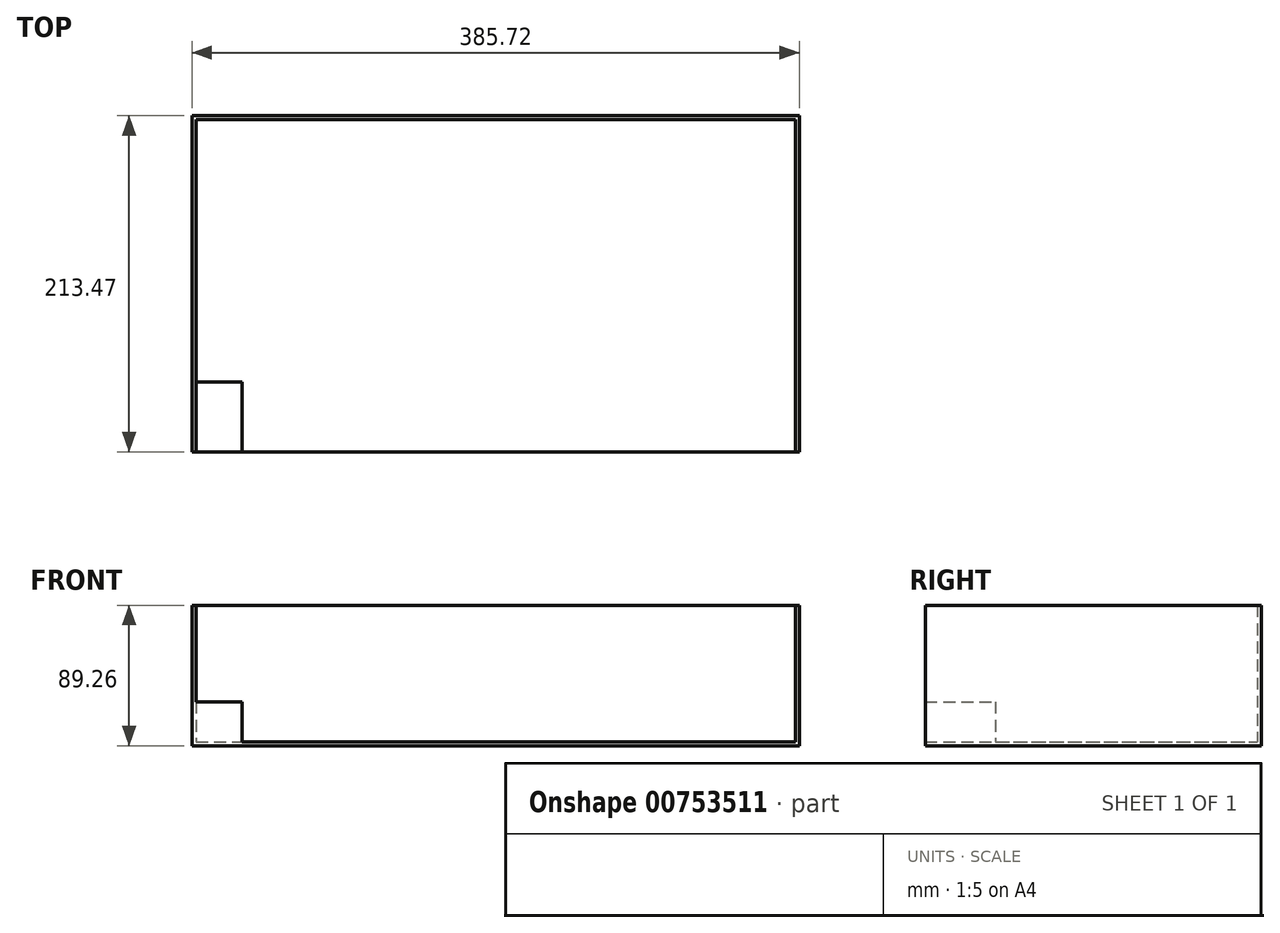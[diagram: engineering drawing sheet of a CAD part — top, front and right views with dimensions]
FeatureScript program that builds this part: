
annotation { "Feature Type Name" : "Feature", "Feature Type Description" : "" }
export const myFeature = defineFeature(function(context is Context, id is Id, definition is map)
    precondition{}
    {
        {
            var Q0;
            Q0=qCreatedBy(makeId("Top.planeOp"),FACE);
            var sketch = newSketch(context, id + "F0", { "sketchPlane" : qUnion([Q0])});
            skLineSegment(sketch, "E0.bottom", {"start": v(192.86, -111.17) * mm, "end": v(-192.86, -111.17) * mm});
            skLineSegment(sketch, "E0.top", {"start": v(192.86, 111.17) * mm, "end": v(-192.86, 111.17) * mm});
            skLineSegment(sketch, "E0.left", {"start": v(192.86, -111.17) * mm, "end": v(192.86, 111.17) * mm});
            skLineSegment(sketch, "E0.right", {"start": v(-192.86, -111.17) * mm, "end": v(-192.86, 111.17) * mm});
            skPoint(sketch, "E0.middle", {"position": v(0, 0) * mm});
            skSolve(sketch);
        }
        {
            var Q0;
            Q0 = qSketchRegion(id + "F0", true);
            extrude(context, id + "F1", {"entities" : qUnion([Q0]), "depth" : 89.26 * mm, "offsetDistance" : 25.4 * mm});
        }
        {
            var Q0;
            Q0=makeQuery(id+"F1.opExtrude","CAP_FACE",FACE,{"disambiguationData":[OSD([sQuery(id+"F0.wireOp",EDGE,"E0.bottom"),sQuery(id+"F0.wireOp",EDGE,"E0.top"),sQuery(id+"F0.wireOp",EDGE,"E0.left"),sQuery(id+"F0.wireOp",EDGE,"E0.right")])],"isStart":false});
            shell(context, id + "F2", {"entities" : qUnion([Q0]), "thickness" : 2.54 * mm});
        }
        {
            var Q0;
            Q0=makeQuery(id+"F1.opExtrude","SWEPT_FACE",FACE,{"disambiguationData":[OSD([sQuery(id+"F0.wireOp",EDGE,"E0.bottom")])]});
            var sketch = newSketch(context, id + "F3", { "sketchPlane" : qUnion([Q0])});
            skLineSegment(sketch, "E1.bottom", {"start": v(192.86, 89.26) * mm, "end": v(-192.86, 89.26) * mm});
            skLineSegment(sketch, "E1.top", {"start": v(192.86, 0) * mm, "end": v(-192.86, 0) * mm});
            skLineSegment(sketch, "E1.left", {"start": v(192.86, 89.26) * mm, "end": v(192.86, 0) * mm});
            skLineSegment(sketch, "E1.right", {"start": v(-192.86, 89.26) * mm, "end": v(-192.86, 0) * mm});
            skSolve(sketch);
        }
        {
            var Q0;
            Q0 = qSketchRegion(id + "F3", true);
            extrude(context, id + "F4", {"entities" : qUnion([Q0]), "operationType" : NewBodyOperationType.REMOVE, "oppositeDirection" : true, "depth" : 8.87 * mm, "offsetDistance" : 25.4 * mm});
        }
        {
            var Q0;
            Q0=makeQuery(id+"F2.opShell","OFFSET_FACE",FACE,{"disambiguationData":[OSD([sQuery(id+"F0.wireOp",EDGE,"E0.bottom"),sQuery(id+"F0.wireOp",EDGE,"E0.top"),sQuery(id+"F0.wireOp",EDGE,"E0.left"),sQuery(id+"F0.wireOp",EDGE,"E0.right")])]});
            var sketch = newSketch(context, id + "F5", { "sketchPlane" : qUnion([Q0])});
            skLineSegment(sketch, "E2.bottom", {"start": v(-190.32, -102.3) * mm, "end": v(-161.02, -102.3) * mm});
            skLineSegment(sketch, "E2.top", {"start": v(-190.32, -57.85) * mm, "end": v(-161.02, -57.85) * mm});
            skLineSegment(sketch, "E2.left", {"start": v(-190.32, -102.3) * mm, "end": v(-190.32, -57.85) * mm});
            skLineSegment(sketch, "E2.right", {"start": v(-161.02, -102.3) * mm, "end": v(-161.02, -57.85) * mm});
            skSolve(sketch);
        }
        {
            var Q0;
            Q0=makeQuery(id+"F5.imprint","IMPRINT",FACE,{"disambiguationData":[TD([[makeQuery(id+"F5.imprint","IMPRINT",EDGE,{"derivedFrom":sQuery(id+"F5.wireOp",EDGE,"E2.bottom")}),1.0]])]});
            extrude(context, id + "F6", {"entities" : qUnion([Q0]), "operationType" : NewBodyOperationType.ADD, "depth" : 25.4 * mm, "offsetDistance" : 25.4 * mm});
        }
    });
